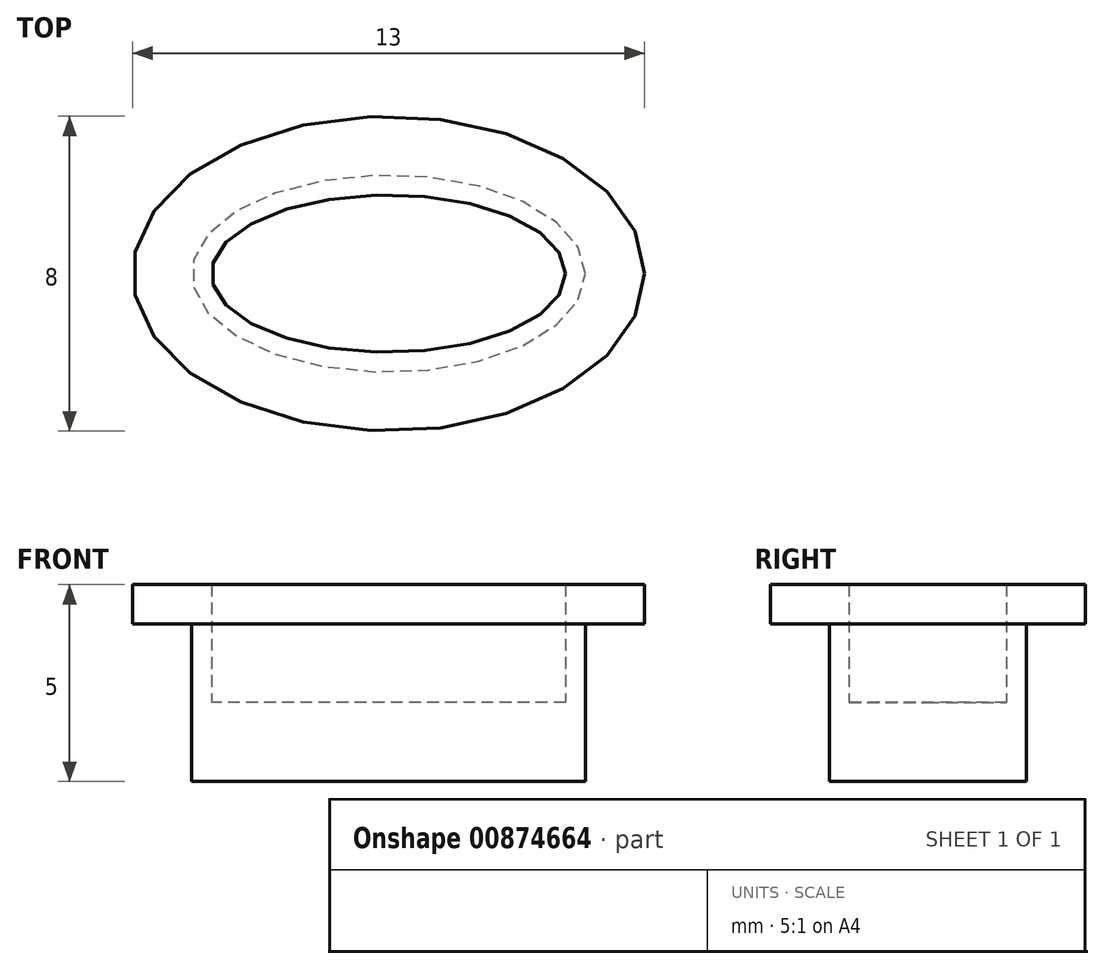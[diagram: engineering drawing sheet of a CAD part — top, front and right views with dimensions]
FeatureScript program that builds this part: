
annotation { "Feature Type Name" : "Feature", "Feature Type Description" : "" }
export const myFeature = defineFeature(function(context is Context, id is Id, definition is map)
    precondition{}
    {
        {
            var Q0;
            Q0=qCreatedBy(makeId("Top.planeOp"),FACE);
            var sketch = newSketch(context, id + "F0", { "sketchPlane" : qUnion([Q0])});
            skEllipse(sketch, "E0", {"center": v(0, 0) * mm, "majorRadius": 6.5 * mm, "minorRadius": 4 * mm, "majorAxis": v(1, 0)});
            skEllipse(sketch, "E1", {"center": v(0, 0) * mm, "majorRadius": 5 * mm, "minorRadius": 2.5 * mm, "majorAxis": v(1, 0)});
            skEllipse(sketch, "E2", {"center": v(0, 0) * mm, "majorRadius": 4.5 * mm, "minorRadius": 2 * mm, "majorAxis": v(1, 0)});
            skSolve(sketch);
        }
        {
            var Q0;
            Q0=makeQuery(id+"F0.imprint","IMPRINT",FACE,{"disambiguationData":[TD([[makeQuery(id+"F0.imprint","IMPRINT",EDGE,{"derivedFrom":sQuery(id+"F0.wireOp",EDGE,"E0")}),1.0]])]});
            var Q1;
            Q1=makeQuery(id+"F0.imprint","IMPRINT",FACE,{"disambiguationData":[TD([[makeQuery(id+"F0.imprint","IMPRINT",EDGE,{"derivedFrom":sQuery(id+"F0.wireOp",EDGE,"E1")}),1.0]])]});
            extrude(context, id + "F1", {"entities" : qUnion([Q0, Q1]), "depth" : 1 * mm, "offsetDistance" : 25 * mm});
        }
        {
            var Q0;
            Q0=makeQuery(id+"F0.imprint","IMPRINT",FACE,{"disambiguationData":[TD([[makeQuery(id+"F0.imprint","IMPRINT",EDGE,{"derivedFrom":sQuery(id+"F0.wireOp",EDGE,"E1")}),1.0]])]});
            var Q1;
            Q1=makeQuery(id+"F0.imprint","IMPRINT",FACE,{"disambiguationData":[TD([[makeQuery(id+"F0.imprint","IMPRINT",EDGE,{"derivedFrom":sQuery(id+"F0.wireOp",EDGE,"E2")}),1.0]])]});
            extrude(context, id + "F2", {"entities" : qUnion([Q0, Q1]), "operationType" : NewBodyOperationType.ADD, "oppositeDirection" : true, "depth" : 4 * mm, "offsetDistance" : 25 * mm});
        }
        {
            var Q0;
            Q0=makeQuery(id+"F0.imprint","IMPRINT",FACE,{"disambiguationData":[TD([[makeQuery(id+"F0.imprint","IMPRINT",EDGE,{"derivedFrom":sQuery(id+"F0.wireOp",EDGE,"E2")}),1.0]])]});
            extrude(context, id + "F3", {"entities" : qUnion([Q0]), "operationType" : NewBodyOperationType.REMOVE, "oppositeDirection" : true, "depth" : 2 * mm, "offsetDistance" : 25 * mm});
        }
    });
